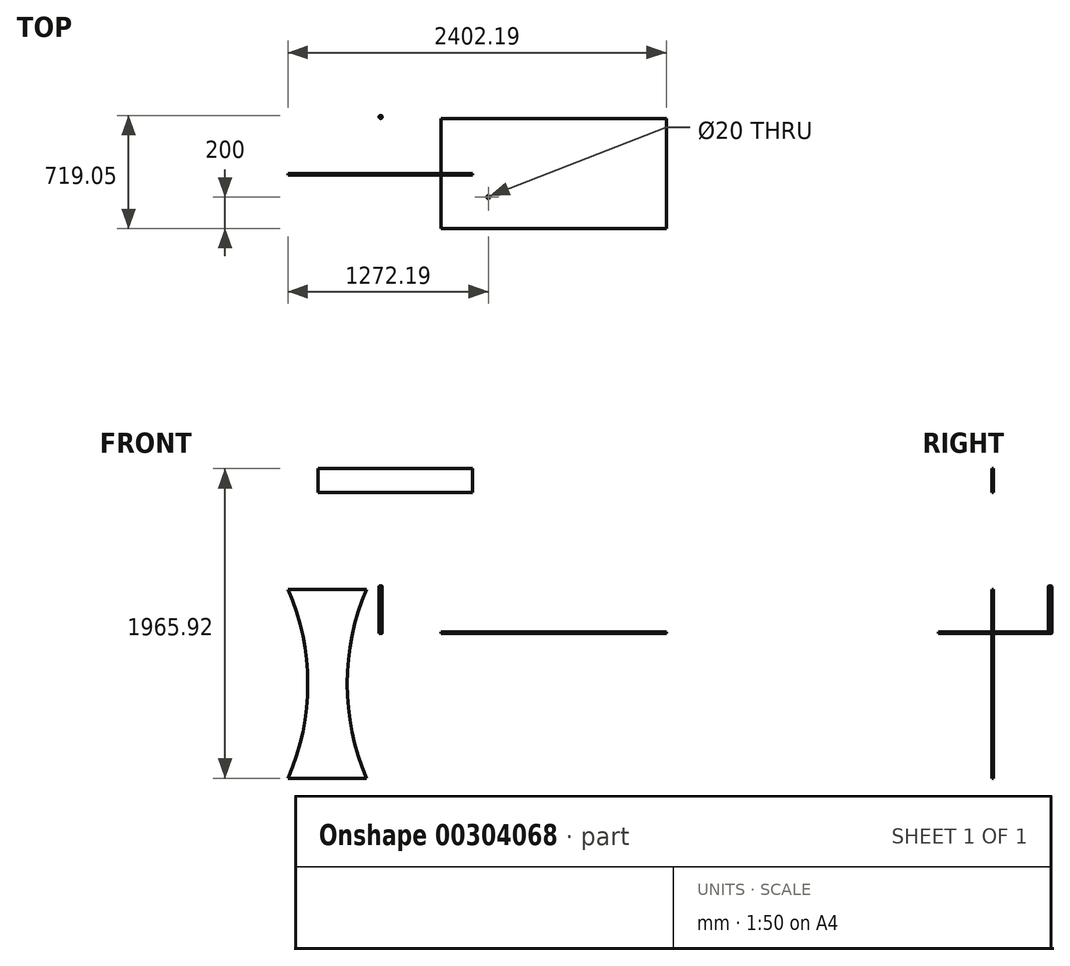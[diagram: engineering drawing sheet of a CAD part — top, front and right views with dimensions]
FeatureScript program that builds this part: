
annotation { "Feature Type Name" : "Feature", "Feature Type Description" : "" }
export const myFeature = defineFeature(function(context is Context, id is Id, definition is map)
    precondition{}
    {
        {
            var Q0;
            Q0=qCreatedBy(makeId("Top.planeOp"),FACE);
            var sketch = newSketch(context, id + "F0", { "sketchPlane" : qUnion([Q0])});
            skLineSegment(sketch, "E0.bottom", {"start": v(715, 350) * mm, "end": v(-715, 350) * mm});
            skLineSegment(sketch, "E0.top", {"start": v(715, -350) * mm, "end": v(-715, -350) * mm});
            skLineSegment(sketch, "E0.left", {"start": v(715, 350) * mm, "end": v(715, -350) * mm});
            skLineSegment(sketch, "E0.right", {"start": v(-715, 350) * mm, "end": v(-715, -350) * mm});
            skPoint(sketch, "E0.middle", {"position": v(0, 0) * mm});
            skCircle(sketch, "E1", {"center": v(-415, -150) * mm, "radius": 10 * mm});
            skSolve(sketch);
        }
        {
            var Q0;
            Q0 = qSketchRegion(id + "F0", true);
            extrude(context, id + "F1", {"entities" : qUnion([Q0]), "depth" : 10 * mm});
        }
        {
            var Q0;
            Q0=qCreatedBy(makeId("Front.planeOp"),FACE);
            var sketch = newSketch(context, id + "F2", { "sketchPlane" : qUnion([Q0])});
            skLineSegment(sketch, "E2.bottom", {"start": v(-1187.19, -919.88) * mm, "end": v(-1687.19, -919.88) * mm});
            skLineSegment(sketch, "E2.top", {"start": v(-1187.19, 280.12) * mm, "end": v(-1687.19, 280.12) * mm});
            skPoint(sketch, "E2.middle", {"position": v(-1437.19, -319.88) * mm});
            skArc(sketch, "E3", {"start": v(-1687.19, -919.88) * mm, "mid": v(-1561.96, -319.88) * mm, "end": v(-1687.19, 280.12) * mm});
            skArc(sketch, "E4", {"start": v(-1187.19, 280.12) * mm, "mid": v(-1312.41, -319.88) * mm, "end": v(-1187.19, -919.88) * mm});
            skSolve(sketch);
        }
        {
            var Q0;
            Q0 = qSketchRegion(id + "F2", true);
            extrude(context, id + "F3", {"entities" : qUnion([Q0]), "depth" : 10 * mm});
        }
        {
            var Q0;
            Q0=qCreatedBy(makeId("Front.planeOp"),FACE);
            var sketch = newSketch(context, id + "F4", { "sketchPlane" : qUnion([Q0])});
            skLineSegment(sketch, "E5.bottom", {"start": v(-516.07, 896.04) * mm, "end": v(-1496.07, 896.04) * mm});
            skLineSegment(sketch, "E5.top", {"start": v(-516.07, 1046.04) * mm, "end": v(-1496.07, 1046.04) * mm});
            skLineSegment(sketch, "E5.left", {"start": v(-516.07, 896.04) * mm, "end": v(-516.07, 1046.04) * mm});
            skLineSegment(sketch, "E5.right", {"start": v(-1496.07, 896.04) * mm, "end": v(-1496.07, 1046.04) * mm});
            skPoint(sketch, "E5.middle", {"position": v(-1006.07, 971.04) * mm});
            skSolve(sketch);
        }
        {
            var Q0;
            Q0=makeQuery(id+"F4.imprint","IMPRINT",FACE,{"disambiguationData":[TD([[makeQuery(id+"F4.imprint","IMPRINT",EDGE,{"derivedFrom":sQuery(id+"F4.wireOp",EDGE,"E5.bottom")}),-1.0]])]});
            extrude(context, id + "F5", {"entities" : qUnion([Q0]), "depth" : 10 * mm});
        }
        {
            var Q0;
            Q0=qCreatedBy(makeId("Top.planeOp"),FACE);
            var sketch = newSketch(context, id + "F6", { "sketchPlane" : qUnion([Q0])});
            skCircle(sketch, "E6", {"center": v(-1099.32, 359.05) * mm, "radius": 10 * mm});
            skSolve(sketch);
        }
        {
            var Q0;
            Q0 = qSketchRegion(id + "F6", true);
            extrude(context, id + "F7", {"entities" : qUnion([Q0]), "depth" : 300 * mm});
        }
        {
            var Q0;
            Q0=makeQuery(id+"F7.opExtrude","CAP_EDGE",EDGE,{"disambiguationData":[OSD([sQuery(id+"F6.wireOp",EDGE,"E6")])],"isStart":false});
            var Q1;
            Q1=makeQuery(id+"F7.opExtrude","CAP_EDGE",EDGE,{"disambiguationData":[OSD([sQuery(id+"F6.wireOp",EDGE,"E6")])],"isStart":true});
            chamfer(context, id + "F8", {"entities" : qUnion([Q0, Q1]), "width" : 1.5 * mm, "tangentPropagation" : true});
        }
    });
